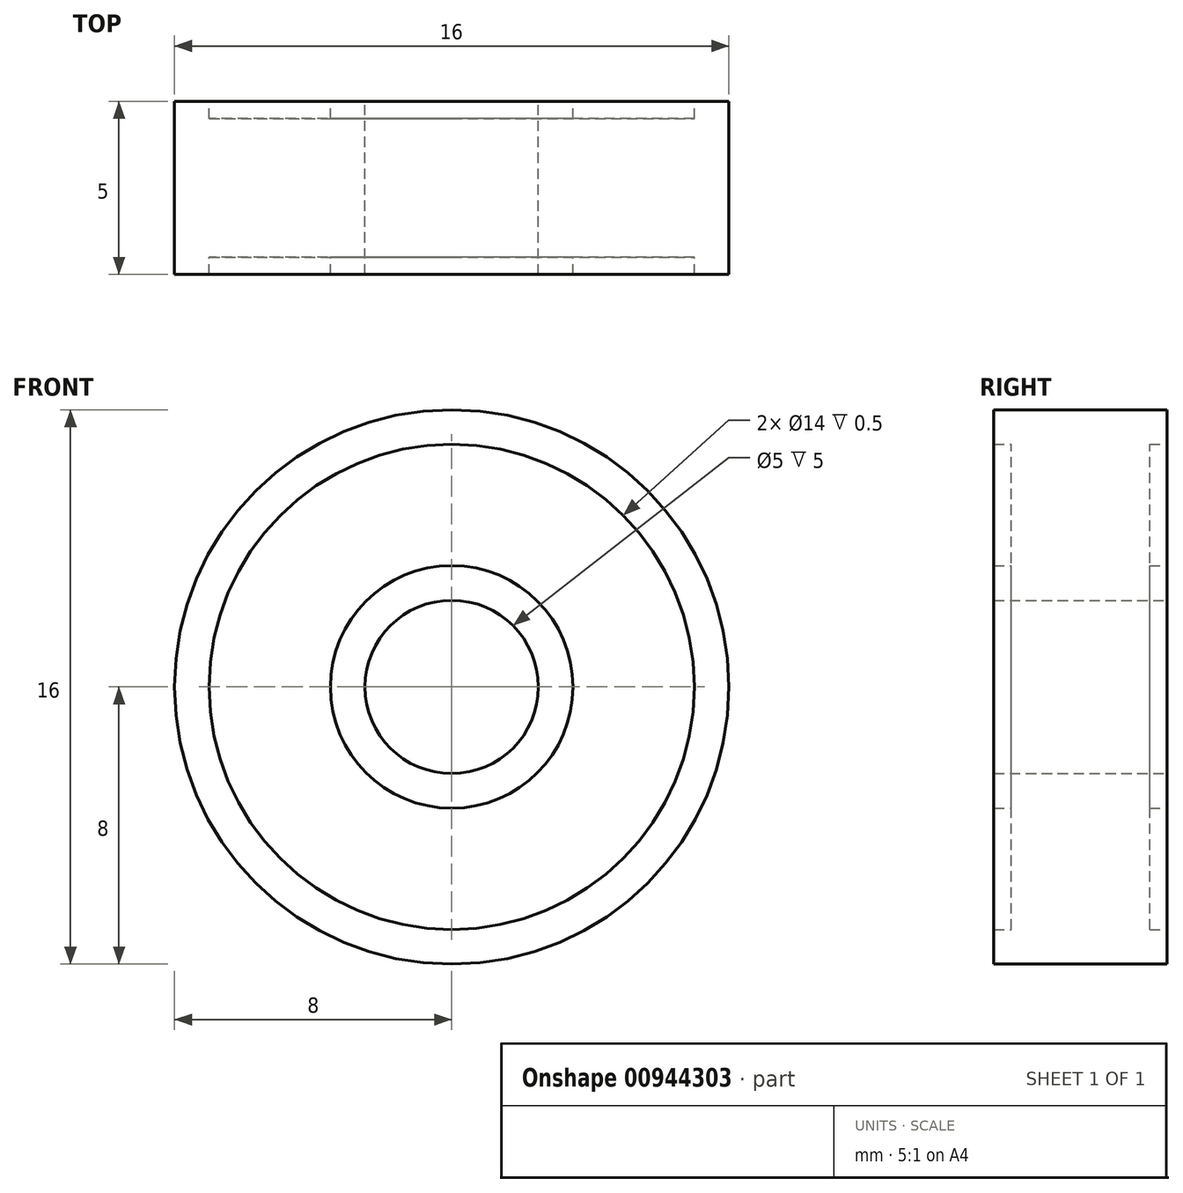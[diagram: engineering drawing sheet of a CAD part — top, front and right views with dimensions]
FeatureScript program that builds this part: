
annotation { "Feature Type Name" : "Feature", "Feature Type Description" : "" }
export const myFeature = defineFeature(function(context is Context, id is Id, definition is map)
    precondition{}
    {
        {
            var Q0;
            Q0=qCreatedBy(makeId("Front.planeOp"),FACE);
            var sketch = newSketch(context, id + "F0", { "sketchPlane" : qUnion([Q0])});
            skCircle(sketch, "E0", {"center": v(0, 0) * mm, "radius": 2.5 * mm});
            skCircle(sketch, "E1", {"center": v(0, 0) * mm, "radius": 8 * mm});
            skCircle(sketch, "E2", {"center": v(0, 0) * mm, "radius": 3.5 * mm});
            skCircle(sketch, "E3", {"center": v(0, 0) * mm, "radius": 7 * mm});
            skSolve(sketch);
        }
        {
            var Q0;
            Q0=makeQuery(id+"F0.imprint","IMPRINT",FACE,{"disambiguationData":[TD([[makeQuery(id+"F0.imprint","IMPRINT",EDGE,{"derivedFrom":sQuery(id+"F0.wireOp",EDGE,"E0")}),-1.0]])]});
            var Q1;
            Q1=makeQuery(id+"F0.imprint","IMPRINT",FACE,{"disambiguationData":[TD([[makeQuery(id+"F0.imprint","IMPRINT",EDGE,{"derivedFrom":sQuery(id+"F0.wireOp",EDGE,"E1")}),1.0]])]});
            extrude(context, id + "F1", {"entities" : qUnion([Q0, Q1]), "depth" : 5 * mm, "offsetDistance" : 25 * mm, "symmetric" : true});
        }
        {
            var Q0;
            Q0=makeQuery(id+"F0.imprint","IMPRINT",FACE,{"disambiguationData":[TD([[makeQuery(id+"F0.imprint","IMPRINT",EDGE,{"derivedFrom":sQuery(id+"F0.wireOp",EDGE,"E2")}),-1.0]])]});
            extrude(context, id + "F2", {"entities" : qUnion([Q0]), "operationType" : NewBodyOperationType.ADD, "depth" : 4 * mm, "offsetDistance" : 25 * mm, "symmetric" : true});
        }
    });
